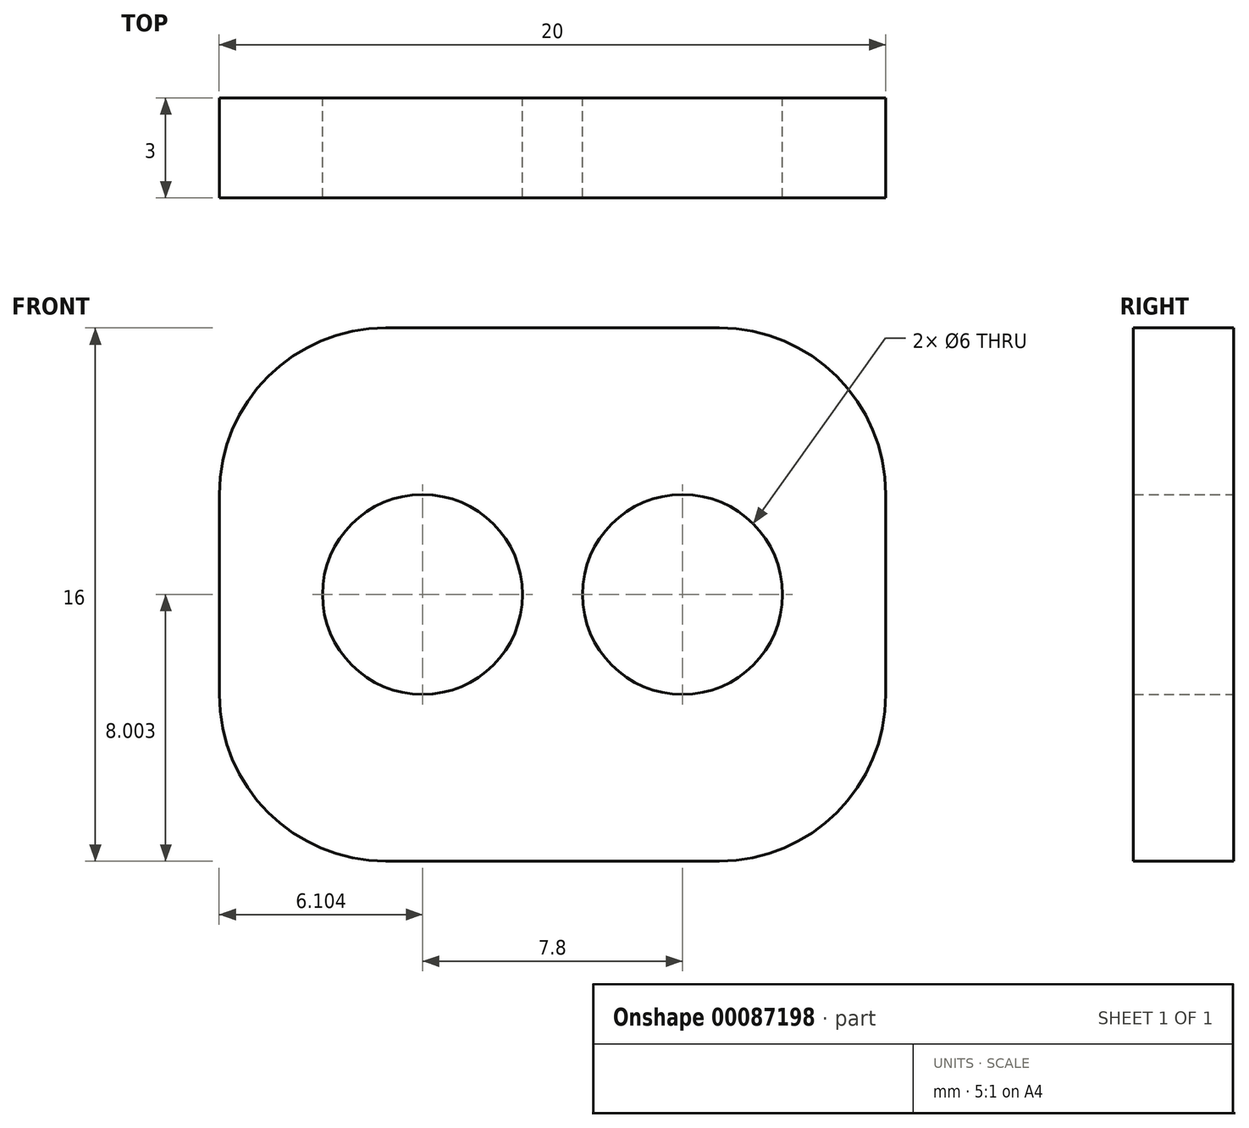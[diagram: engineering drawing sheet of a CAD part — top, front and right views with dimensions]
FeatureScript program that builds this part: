
annotation { "Feature Type Name" : "Feature", "Feature Type Description" : "" }
export const myFeature = defineFeature(function(context is Context, id is Id, definition is map)
    precondition{}
    {
        {
            var Q0;
            Q0=qCreatedBy(makeId("Front.planeOp"),FACE);
            var sketch = newSketch(context, id + "F0", { "sketchPlane" : qUnion([Q0])});
            skLineSegment(sketch, "E0", {"start": v(-151.84, 33.38) * mm, "end": v(-144.04, 33.38) * mm, "construction": true});
            skCircle(sketch, "E1", {"center": v(-151.84, 33.38) * mm, "radius": 3 * mm});
            skCircle(sketch, "E2", {"center": v(-144.04, 33.38) * mm, "radius": 3 * mm});
            skLineSegment(sketch, "E3.bottom", {"start": v(-142.94, 41.38) * mm, "end": v(-152.94, 41.38) * mm});
            skLineSegment(sketch, "E3.top", {"start": v(-142.94, 25.38) * mm, "end": v(-152.94, 25.38) * mm});
            skLineSegment(sketch, "E3.left", {"start": v(-137.94, 36.38) * mm, "end": v(-137.94, 30.38) * mm});
            skLineSegment(sketch, "E3.right", {"start": v(-157.94, 36.38) * mm, "end": v(-157.94, 30.38) * mm});
            skPoint(sketch, "E3.middle", {"position": v(-147.94, 33.38) * mm});
            skPoint(sketch, "E4.visualSharp", {"position": v(-137.94, 41.38) * mm});
            skArc(sketch, "E4.filletArc", {"start": v(-137.94, 36.38) * mm, "mid": v(-139.4, 39.92) * mm, "end": v(-142.94, 41.38) * mm});
            skPoint(sketch, "E5.visualSharp", {"position": v(-137.94, 25.38) * mm});
            skArc(sketch, "E5.filletArc", {"start": v(-142.94, 25.38) * mm, "mid": v(-139.4, 26.85) * mm, "end": v(-137.94, 30.38) * mm});
            skPoint(sketch, "E6.visualSharp", {"position": v(-157.94, 25.38) * mm});
            skArc(sketch, "E6.filletArc", {"start": v(-157.94, 30.38) * mm, "mid": v(-156.47, 26.85) * mm, "end": v(-152.94, 25.38) * mm});
            skPoint(sketch, "E7.visualSharp", {"position": v(-157.94, 41.38) * mm});
            skArc(sketch, "E7.filletArc", {"start": v(-152.94, 41.38) * mm, "mid": v(-156.47, 39.92) * mm, "end": v(-157.94, 36.38) * mm});
            skSolve(sketch);
        }
        {
            var Q0;
            Q0=qSketchRegion(id+"F0",true);
            extrude(context, id + "F1", {"entities" : qUnion([Q0]), "depth" : 3 * mm});
        }
    });
